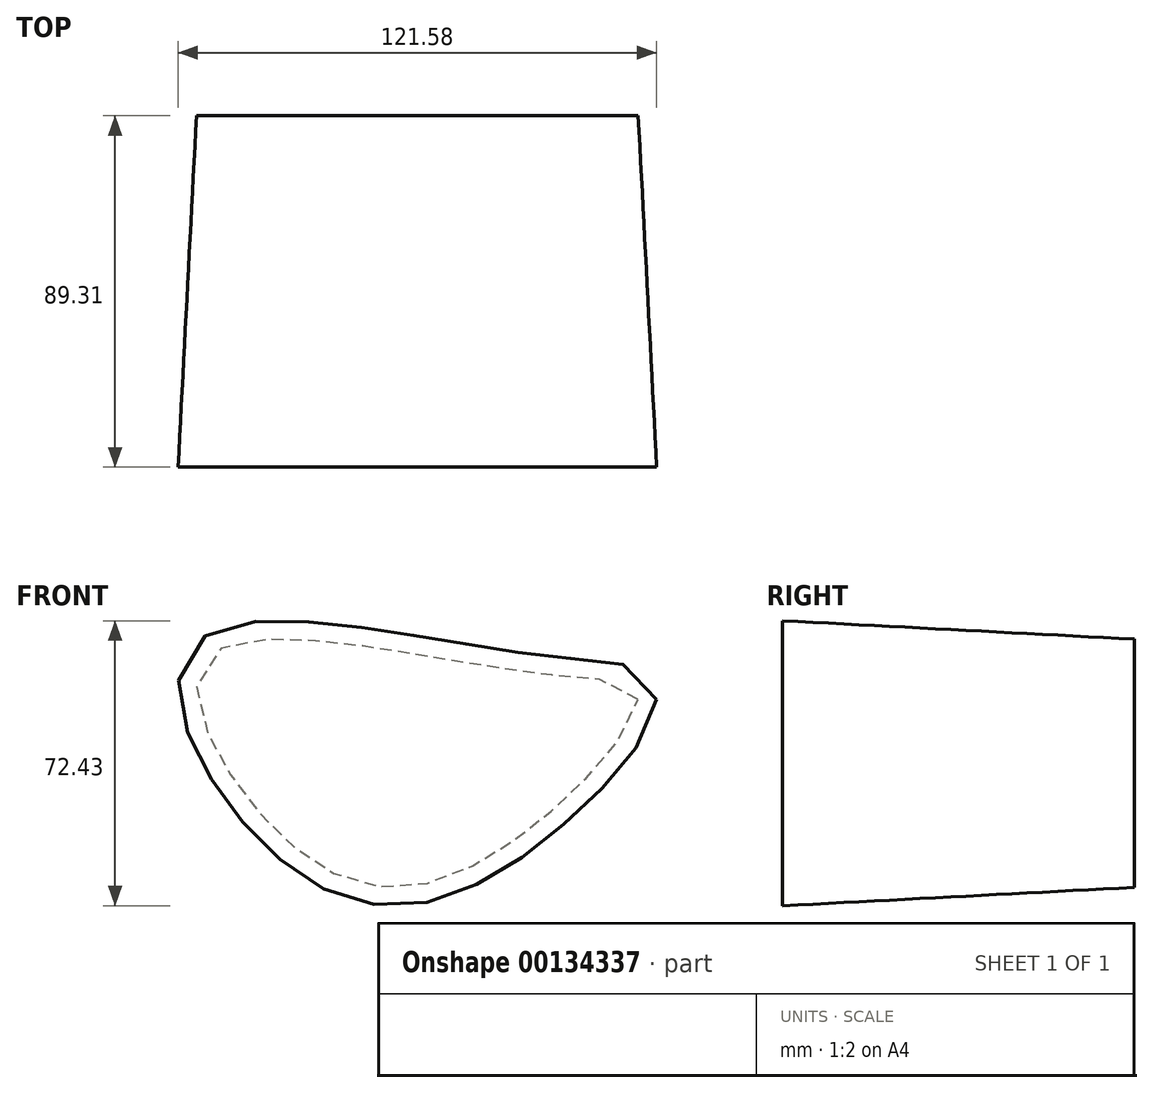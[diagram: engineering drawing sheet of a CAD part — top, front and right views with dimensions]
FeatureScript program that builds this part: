
annotation { "Feature Type Name" : "Feature", "Feature Type Description" : "" }
export const myFeature = defineFeature(function(context is Context, id is Id, definition is map)
    precondition{}
    {
        {
            var Q0;
            Q0=qCreatedBy(makeId("Front.planeOp"),FACE);
            var sketch = newSketch(context, id + "F0", { "sketchPlane" : qUnion([Q0])});
            skFitSpline(sketch, "E0", {"points": [v(-53.28, 52.08) * mm, v(-30.9, 4.72) * mm, v(15.17, 0) * mm, v(56.8, 42.09) * mm, v(31.63, 48.56) * mm, v(-53.28, 52.08) * mm]});
            skSolve(sketch);
        }
        {
            var Q0;
            Q0 = qSketchRegion(id + "F0", true);
            var Q1;
            Q1=makeQuery(id+"F0.imprint","IMPRINT",FACE,{"disambiguationData":[TD([[makeQuery(id+"F0.imprint","IMPRINT",EDGE,{"derivedFrom":sQuery(id+"F0.wireOp",EDGE,"E0")}),1.0]])]});
            extrude(context, id + "F1", {"entities" : qUnion([Q0, Q1]), "depth" : 89.3 * mm, "hasDraft" : true, "draftAngle" : 3 * degree});
        }
    });
